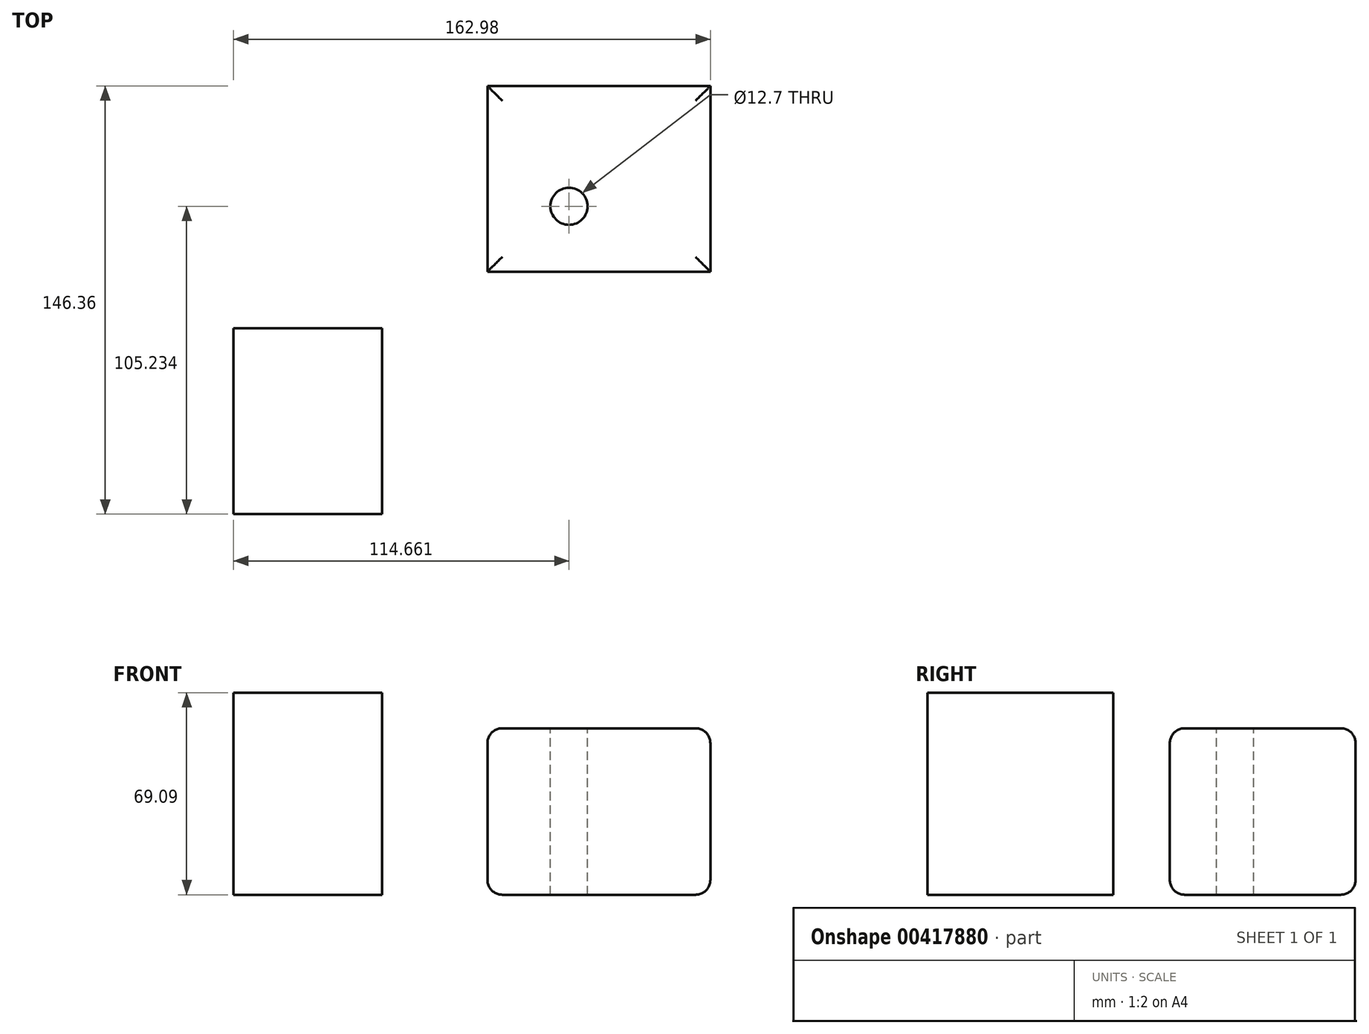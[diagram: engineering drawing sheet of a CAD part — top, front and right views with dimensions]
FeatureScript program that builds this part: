
annotation { "Feature Type Name" : "Feature", "Feature Type Description" : "" }
export const myFeature = defineFeature(function(context is Context, id is Id, definition is map)
    precondition{}
    {
        {
            var Q0;
            Q0=qCreatedBy(makeId("Top.planeOp"),FACE);
            var sketch = newSketch(context, id + "F0", { "sketchPlane" : qUnion([Q0])});
            skLineSegment(sketch, "E0", {"start": v(0, 54.12) * mm, "end": v(0, -45.3) * mm, "construction": true});
            skLineSegment(sketch, "E1", {"start": v(-54.25, 0) * mm, "end": v(54.75, 0) * mm, "construction": true});
            skLineSegment(sketch, "E2", {"start": v(0, 31.75) * mm, "end": v(38.1, 31.75) * mm});
            skLineSegment(sketch, "E3", {"start": v(38.1, 31.75) * mm, "end": v(38.1, 0) * mm});
            skLineSegment(sketch, "E4.MirrorCS", {"start": v(0, 31.75) * mm, "end": v(-38.1, 31.75) * mm});
            skLineSegment(sketch, "E5.MirrorCS", {"start": v(-38.1, 31.75) * mm, "end": v(-38.1, 0) * mm});
            skLineSegment(sketch, "E6.MirrorCS", {"start": v(0, -31.75) * mm, "end": v(38.1, -31.75) * mm});
            skLineSegment(sketch, "E7.MirrorCS", {"start": v(38.1, -31.75) * mm, "end": v(38.1, 0) * mm});
            skLineSegment(sketch, "E8.MirrorCS", {"start": v(-38.1, -31.75) * mm, "end": v(-38.1, 0) * mm});
            skLineSegment(sketch, "E9.MirrorCS", {"start": v(0, -31.75) * mm, "end": v(-38.1, -31.75) * mm});
            skSolve(sketch);
        }
        {
            var Q0;
            Q0=makeQuery(id+"F0.imprint","IMPRINT",FACE,{"disambiguationData":[TD([[makeQuery(id+"F0.imprint","IMPRINT",EDGE,{"derivedFrom":sQuery(id+"F0.wireOp",EDGE,"E3")}),-1.0]])]});
            extrude(context, id + "F1", {"entities" : qUnion([Q0]), "depth" : 56.9 * mm});
        }
        {
            var Q0;
            Q0=makeQuery(id+"F1.opExtrude","CAP_FACE",FACE,{"disambiguationData":[OSD([sQuery(id+"F0.wireOp",EDGE,"E3"),sQuery(id+"F0.wireOp",EDGE,"E2"),sQuery(id+"F0.wireOp",EDGE,"E5.MirrorCS"),sQuery(id+"F0.wireOp",EDGE,"E4.MirrorCS"),sQuery(id+"F0.wireOp",EDGE,"E6.MirrorCS"),sQuery(id+"F0.wireOp",EDGE,"E7.MirrorCS"),sQuery(id+"F0.wireOp",EDGE,"E8.MirrorCS"),sQuery(id+"F0.wireOp",EDGE,"E9.MirrorCS")])],"isStart":false});
            var Q1;
            Q1=makeQuery(id+"F1.opExtrude","CAP_FACE",FACE,{"disambiguationData":[OSD([sQuery(id+"F0.wireOp",EDGE,"E3"),sQuery(id+"F0.wireOp",EDGE,"E2"),sQuery(id+"F0.wireOp",EDGE,"E5.MirrorCS"),sQuery(id+"F0.wireOp",EDGE,"E4.MirrorCS"),sQuery(id+"F0.wireOp",EDGE,"E6.MirrorCS"),sQuery(id+"F0.wireOp",EDGE,"E7.MirrorCS"),sQuery(id+"F0.wireOp",EDGE,"E8.MirrorCS"),sQuery(id+"F0.wireOp",EDGE,"E9.MirrorCS")])],"isStart":true});
            fillet(context, id + "F2", {"entities" : qUnion([Q0, Q1]), "radius" : 5.08 * mm, "tangentPropagation" : true, "allowEdgeOverflow" : false});
        }
        {
            var Q0;
            Q0=makeQuery(id+"F1.opExtrude","CAP_FACE",FACE,{"disambiguationData":[OSD([sQuery(id+"F0.wireOp",EDGE,"E3"),sQuery(id+"F0.wireOp",EDGE,"E2"),sQuery(id+"F0.wireOp",EDGE,"E5.MirrorCS"),sQuery(id+"F0.wireOp",EDGE,"E4.MirrorCS"),sQuery(id+"F0.wireOp",EDGE,"E6.MirrorCS"),sQuery(id+"F0.wireOp",EDGE,"E7.MirrorCS"),sQuery(id+"F0.wireOp",EDGE,"E8.MirrorCS"),sQuery(id+"F0.wireOp",EDGE,"E9.MirrorCS")])],"isStart":false});
            var sketch = newSketch(context, id + "F3", { "sketchPlane" : qUnion([Q0])});
            skPoint(sketch, "E10", {"position": v(-10.22, -9.38) * mm});
            skSolve(sketch);
        }
        {
            var Q0;
            Q0=sQuery(id+"F3.wireOp",VERTEX,"E10");
            var Q1;
            Q1=makeQuery(id+"F1.opExtrude","SWEPT_BODY",BODY,{"disambiguationData":[OSD([sQuery(id+"F0.wireOp",EDGE,"E3"),sQuery(id+"F0.wireOp",EDGE,"E2"),sQuery(id+"F0.wireOp",EDGE,"E5.MirrorCS"),sQuery(id+"F0.wireOp",EDGE,"E4.MirrorCS"),sQuery(id+"F0.wireOp",EDGE,"E6.MirrorCS"),sQuery(id+"F0.wireOp",EDGE,"E7.MirrorCS"),sQuery(id+"F0.wireOp",EDGE,"E8.MirrorCS"),sQuery(id+"F0.wireOp",EDGE,"E9.MirrorCS")])]});
            hole(context, id + "F4", {"style" : HoleStyle.SIMPLE, "endStyle" : HoleEndStyle.THROUGH, "holeDiameter" : 12.7 * mm, "isTappedThrough" : true, "tappedDepth" : 12.7 * mm, "tapClearance" : 3, "locations" : qUnion([Q0]), "scope" : qUnion([Q1])});
        }
        {
            var Q0;
            Q0=qCreatedBy(makeId("Top.planeOp"),FACE);
            var sketch = newSketch(context, id + "F5", { "sketchPlane" : qUnion([Q0])});
            skLineSegment(sketch, "E11.bottom", {"start": v(-74.08, -51.11) * mm, "end": v(-124.88, -51.11) * mm});
            skLineSegment(sketch, "E11.top", {"start": v(-74.08, -114.61) * mm, "end": v(-124.88, -114.61) * mm});
            skLineSegment(sketch, "E11.left", {"start": v(-74.08, -51.11) * mm, "end": v(-74.08, -114.61) * mm});
            skLineSegment(sketch, "E11.right", {"start": v(-124.88, -51.11) * mm, "end": v(-124.88, -114.61) * mm});
            skSolve(sketch);
        }
        {
            var Q0;
            Q0=makeQuery(id+"F5.imprint","IMPRINT",FACE,{"disambiguationData":[TD([[makeQuery(id+"F5.imprint","IMPRINT",EDGE,{"derivedFrom":sQuery(id+"F5.wireOp",EDGE,"E11.bottom")}),1.0]])]});
            extrude(context, id + "F6", {"entities" : qUnion([Q0]), "depth" : 69.1 * mm});
        }
    });
